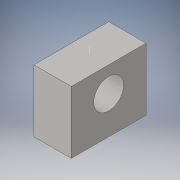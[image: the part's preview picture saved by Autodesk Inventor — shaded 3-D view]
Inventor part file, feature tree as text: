
AUTODESK INVENTOR PART (.ipt)
format: ipt  version: 2016 (Build 200138000, 138)  size: 113,152 bytes
history: native  units: in
note: dims shown in document units (in); Inventor stores cm internally (conversion verified against a paired STEP export)
features: extrude x1, hole x1, other x1, sketch x1
ambient origin geometry x8: Origin, YZ Plane, XZ Plane, XY Plane, X Axis, Y Axis, Z Axis, Center Point
bodies: Solid1 (feature_tree)
feature tree (4):
  extrude  "Extrusion1"  Depth=0.1181in
  hole  "Hole1"  [1 undecoded]
  other  "base+body"
  sketch  "Sketch3"  dims[d0=0.1575in d1=0.1181in d2=0.0591in d3=0.0413in d4=0.1181in d5=0.0413in d6=0.0787in d7=0.0984in d8=0.0in d9=0.0591in d10=0.1181in d11=0.0984in d12=0.0591in d13=0.0472in d14=0.75in d15=0.375in d16=0.25in d17=0.5635in d18=1.0in d19=0.8108in]
note: 1 required parameter value undecoded (feature->parameter linkage not recoverable at this tier; creation-order binding heuristic only, values carry confidence <= 0.55)
